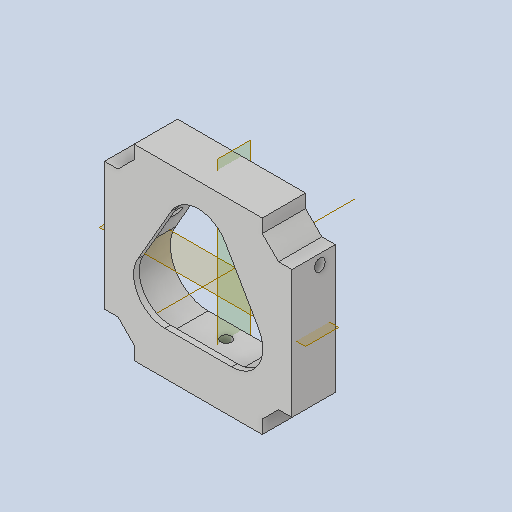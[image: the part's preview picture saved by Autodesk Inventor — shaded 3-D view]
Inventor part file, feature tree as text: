
AUTODESK INVENTOR PART (.ipt)
format: ipt  version: 2023 (Build 270158000, 158)  size: 269,312 bytes
history: native  units: mm
features: other x12, reference x12, extrude x5, sketch x5, plane x3, projected_geometry x3, pattern_circular x1
ambient origin geometry x8: Origin, YZ Plane, XZ Plane, XY Plane, X Axis, Y Axis, Z Axis, Center Point
bodies: Body1 (feature_tree)
feature tree (41):
  plane  "Work Plane1"
  extrude  "Extrusion1"  Depth=10.0mm
  extrude  "IM_offset"  Depth=53.8mm
  plane  "Arbeitsebene5"
  plane  "Arbeitsebene6"
  extrude  "Extrusion27"  Depth=45.0mm
  extrude  "Extrusion28"  Depth=20.0mm
  sketch  "Sketch35"  dims[d32=2.8mm d33=2.8mm d34=2.8mm d35=3.0mm d36=0.1mm d37=0.1mm d38=0.1mm d39=0.1mm d40=0.2mm d41=10.0mm d42=0.0mm d184=0.1mm d185=0.0mm d186=10.0mm d187=10.0mm d188=0.0mm d189=0.1mm d190=1.5mm d191=0.0mm d192=2.8mm d203=30.0mm d204=0.0mm d205=30.0mm d206=360.0deg d160=0.5mm d161=0.872665mm d162=0.5mm d163=0.872665mm]
  other  "Work Axis1"
  extrude  "Extrusion29"  Depth=1.5mm
  pattern_circular  "Circular Pattern2"  [2 undecoded]
  sketch  "Sketch1"  dims[d10=10.0mm d11=0.0mm d18=53.8mm]
  reference  "Reference1"
  reference  "Reference2"
  reference  "Reference3"
  reference  "Reference4"
  reference  "Reference9"
  reference  "Reference20"
  reference  "Reference21"
  reference  "Reference22"
  reference  "Reference23"
  reference  "Reference24"
  sketch  "Skizze4"  dims[d19=45.0deg d20=53.8mm]
  projected_geometry  "Projizierte Kontur1"
  sketch  "Sketch33"  dims[d21=45.0mm d22=45.0mm]
  reference  "Reference35"
  sketch  "Sketch34"  dims[d30=20.0mm d31=20.0mm]
  projected_geometry  "Projected Loop18"
  reference  "Reference36"
  projected_geometry  "Projected Loop19"
  other  "Assembly_Cube_v2_Thorlabs.iam"
  other  "10_Cube_Base:1"
  other  "00_Base_v0:1"
  other  "Assembly_Cube_Kinematic_Mirrormount_v2.iam"
  other  "Assembly_Cube_empty_1x1_v2:1"
  other  "10_Cube_1x1_v2:1"
  other  "10_Lid_1x1_v2:1"
  other  "<userpath> Lab\Documents\UC2-INVENTOR-Git\uc2_v3\Assembly_Cube_Thorlabs_Cage_v3.iam"
  other  "Assembly_Cube_Thorlabs_Cage_v3.iam"
  other  "00_THORLABS_AC254-050-A-ML-Step:1"
  other  "10_Cube_Lid:1"
note: 2 required parameter values undecoded (feature->parameter linkage not recoverable at this tier; creation-order binding heuristic only, values carry confidence <= 0.55)
